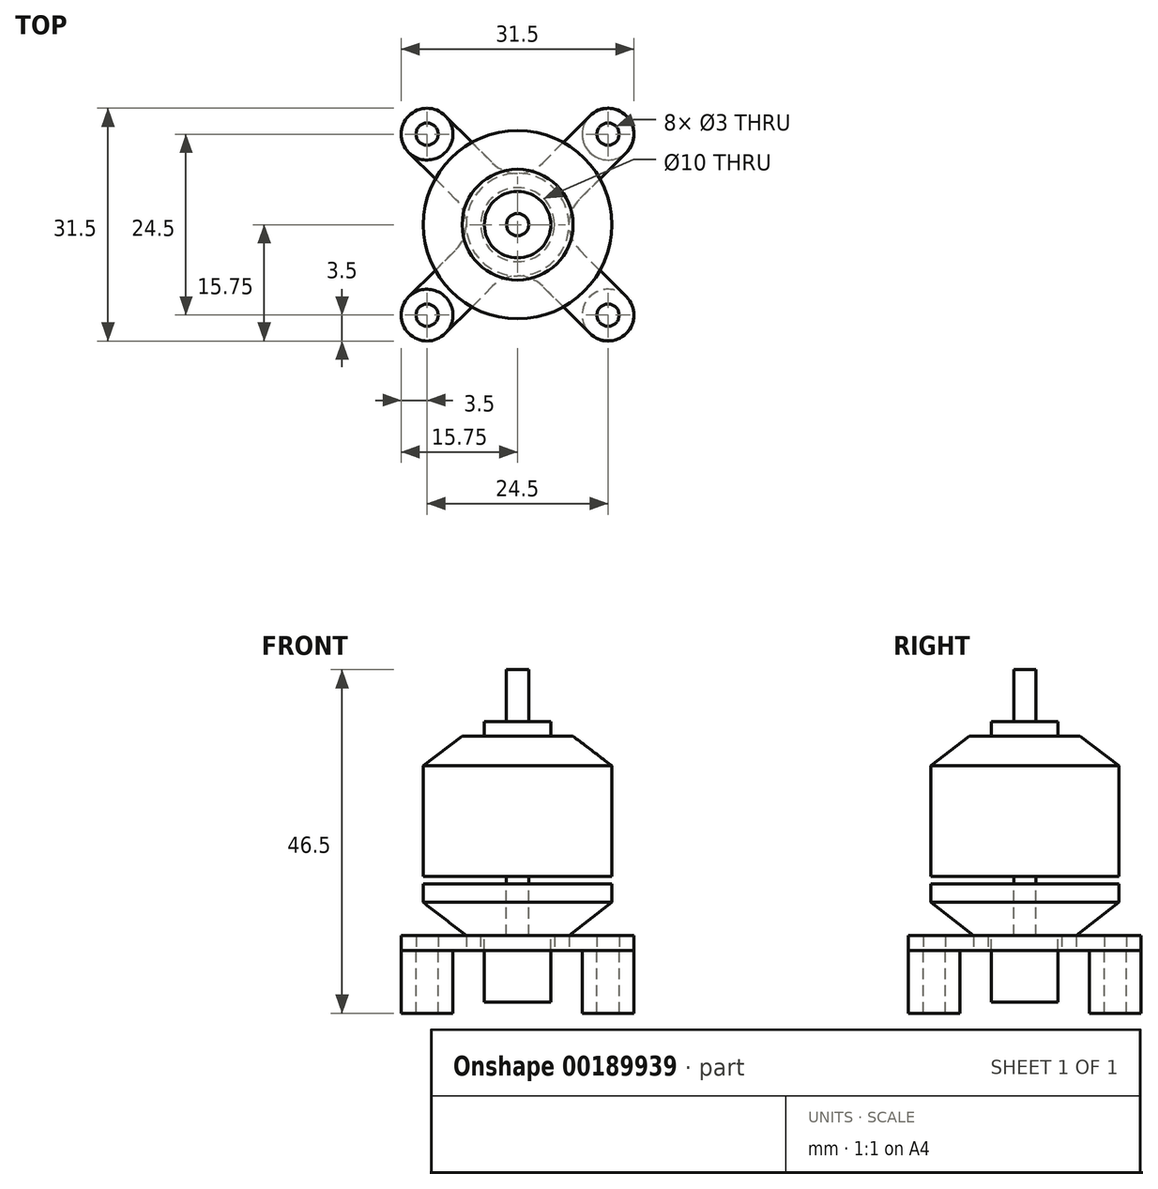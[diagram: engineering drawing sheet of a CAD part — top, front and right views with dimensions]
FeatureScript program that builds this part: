
annotation { "Feature Type Name" : "Feature", "Feature Type Description" : "" }
export const myFeature = defineFeature(function(context is Context, id is Id, definition is map)
    precondition{}
    {
        {
            var Q0;
            Q0=qCreatedBy(makeId("Top.planeOp"),FACE);
            var sketch = newSketch(context, id + "F0", { "sketchPlane" : qUnion([Q0])});
            skLineSegment(sketch, "E0", {"start": v(3.41, 8.36) * mm, "end": v(9.78, 14.72) * mm});
            skLineSegment(sketch, "E1", {"start": v(14.72, 9.78) * mm, "end": v(8.36, 3.41) * mm});
            skArc(sketch, "E2", {"start": v(9.78, 14.72) * mm, "mid": v(14.72, 14.72) * mm, "end": v(14.72, 9.78) * mm});
            skCircle(sketch, "E3", {"center": v(12.25, 12.25) * mm, "radius": 1.5 * mm});
            skLineSegment(sketch, "E4", {"start": v(12.25, 12.25) * mm, "end": v(12.25, 0) * mm, "construction": true});
            skLineSegment(sketch, "E5", {"start": v(12.25, 12.25) * mm, "end": v(0, 12.25) * mm, "construction": true});
            skLineSegment(sketch, "E6.1.0", {"start": v(-8.36, 3.41) * mm, "end": v(-14.72, 9.78) * mm});
            skArc(sketch, "E6.1.1", {"start": v(-14.72, 9.78) * mm, "mid": v(-14.72, 14.72) * mm, "end": v(-9.78, 14.72) * mm});
            skLineSegment(sketch, "E6.1.2", {"start": v(-9.78, 14.72) * mm, "end": v(-3.41, 8.36) * mm});
            skCircle(sketch, "E6.1.3", {"center": v(-12.25, 12.25) * mm, "radius": 1.5 * mm});
            skLineSegment(sketch, "E6.2.0", {"start": v(-3.41, -8.36) * mm, "end": v(-9.78, -14.72) * mm});
            skArc(sketch, "E6.2.1", {"start": v(-9.78, -14.72) * mm, "mid": v(-14.72, -14.72) * mm, "end": v(-14.72, -9.78) * mm});
            skLineSegment(sketch, "E6.2.2", {"start": v(-14.72, -9.78) * mm, "end": v(-8.36, -3.41) * mm});
            skCircle(sketch, "E6.2.3", {"center": v(-12.25, -12.25) * mm, "radius": 1.5 * mm});
            skLineSegment(sketch, "E6.3.0", {"start": v(8.36, -3.41) * mm, "end": v(14.72, -9.78) * mm});
            skArc(sketch, "E6.3.1", {"start": v(14.72, -9.78) * mm, "mid": v(14.72, -14.72) * mm, "end": v(9.78, -14.72) * mm});
            skLineSegment(sketch, "E6.3.2", {"start": v(9.78, -14.72) * mm, "end": v(3.41, -8.36) * mm});
            skCircle(sketch, "E6.3.3", {"center": v(12.25, -12.25) * mm, "radius": 1.5 * mm});
            skPoint(sketch, "E6.center", {"position": v(0, 0) * mm});
            skCircle(sketch, "E7", {"center": v(0, 0) * mm, "radius": 5 * mm});
            skPoint(sketch, "E8.visualSharp", {"position": v(0, 4.95) * mm});
            skArc(sketch, "E8.filletArc", {"start": v(-3.41, 8.36) * mm, "mid": v(0, 6.95) * mm, "end": v(3.41, 8.36) * mm});
            skPoint(sketch, "E9.visualSharp", {"position": v(4.95, 0) * mm});
            skArc(sketch, "E9.filletArc", {"start": v(8.36, 3.41) * mm, "mid": v(6.95, 0) * mm, "end": v(8.36, -3.41) * mm});
            skPoint(sketch, "E10.visualSharp", {"position": v(0, -4.95) * mm});
            skArc(sketch, "E10.filletArc", {"start": v(3.41, -8.36) * mm, "mid": v(0, -6.95) * mm, "end": v(-3.41, -8.36) * mm});
            skPoint(sketch, "E11.visualSharp", {"position": v(-4.95, 0) * mm});
            skArc(sketch, "E11.filletArc", {"start": v(-8.36, -3.41) * mm, "mid": v(-6.95, 0) * mm, "end": v(-8.36, 3.41) * mm});
            skSolve(sketch);
        }
        {
            var Q0;
            Q0=makeQuery(id+"F0.imprint","IMPRINT",FACE,{"disambiguationData":[TD([[makeQuery(id+"F0.imprint","IMPRINT",EDGE,{"derivedFrom":sQuery(id+"F0.wireOp",EDGE,"E0")}),-1.0]])]});
            extrude(context, id + "F1", {"entities" : qUnion([Q0]), "depth" : 2 * mm});
        }
        {
            var Q0;
            Q0=qCreatedBy(makeId("Front.planeOp"),FACE);
            var sketch = newSketch(context, id + "F2", { "sketchPlane" : qUnion([Q0])});
            skLineSegment(sketch, "E12", {"start": v(12.75, 25) * mm, "end": v(12.75, 10) * mm});
            skLineSegment(sketch, "E13", {"start": v(12.75, 10) * mm, "end": v(1.5, 10) * mm});
            skLineSegment(sketch, "E14", {"start": v(1.5, 10) * mm, "end": v(1.5, 2) * mm});
            skLineSegment(sketch, "E15", {"start": v(1.5, 2) * mm, "end": v(4.5, 2) * mm});
            skLineSegment(sketch, "E16", {"start": v(4.5, 2) * mm, "end": v(4.5, -7) * mm});
            skLineSegment(sketch, "E17", {"start": v(4.5, -7) * mm, "end": v(0, -7) * mm});
            skLineSegment(sketch, "E18", {"start": v(1.5, 31) * mm, "end": v(4.5, 31) * mm});
            skLineSegment(sketch, "E19", {"start": v(4.5, 31) * mm, "end": v(4.5, 29) * mm});
            skLineSegment(sketch, "E20", {"start": v(4.5, 29) * mm, "end": v(7.5, 29) * mm});
            skLineSegment(sketch, "E21", {"start": v(7.5, 29) * mm, "end": v(12.75, 25) * mm});
            skLineSegment(sketch, "E22", {"start": v(0, 38) * mm, "end": v(1.5, 38) * mm});
            skLineSegment(sketch, "E23", {"start": v(1.5, 38) * mm, "end": v(1.5, 31) * mm});
            skLineSegment(sketch, "E24", {"start": v(0, 38) * mm, "end": v(0, -7) * mm});
            skSolve(sketch);
        }
        {
            var Q0;
            Q0=makeQuery(id+"F2.imprint","IMPRINT",FACE,{"disambiguationData":[TD([[makeQuery(id+"F2.imprint","IMPRINT",EDGE,{"derivedFrom":sQuery(id+"F2.wireOp",EDGE,"E12")}),-1.0]])]});
            var Q1;
            Q1=sQuery(id+"F2.wireOp",EDGE,"E24");
            revolve(context, id + "F3", {"entities" : qUnion([Q0]), "axis" : qUnion([Q1]), "revolveType" : RevolveType.FULL});
        }
        {
            var Q0;
            Q0=qCreatedBy(makeId("Front.planeOp"),FACE);
            var sketch = newSketch(context, id + "F4", { "sketchPlane" : qUnion([Q0])});
            skLineSegment(sketch, "E25", {"start": v(0, 9) * mm, "end": v(12.75, 9) * mm});
            skLineSegment(sketch, "E26", {"start": v(12.75, 9) * mm, "end": v(12.75, 6.5) * mm});
            skLineSegment(sketch, "E27", {"start": v(12.75, 6.5) * mm, "end": v(6.95, 2) * mm});
            skLineSegment(sketch, "E28", {"start": v(6.95, 2) * mm, "end": v(0, 2) * mm});
            skLineSegment(sketch, "E29", {"start": v(0, 2) * mm, "end": v(0, 9) * mm});
            skLineSegment(sketch, "E30", {"start": v(12.75, 25) * mm, "end": v(12.75, 10) * mm, "construction": true});
            skLineSegment(sketch, "E31", {"start": v(-12.75, 10) * mm, "end": v(-12.75, 25) * mm, "construction": true});
            skPoint(sketch, "E32.0", {"position": v(6.95, 2) * mm});
            skSolve(sketch);
        }
        {
            var Q0;
            Q0=makeQuery(id+"F4.imprint","IMPRINT",FACE,{"disambiguationData":[TD([[makeQuery(id+"F4.imprint","IMPRINT",EDGE,{"derivedFrom":sQuery(id+"F4.wireOp",EDGE,"E25")}),-1.0]])]});
            var Q1;
            Q1=sQuery(id+"F4.wireOp",EDGE,"E29");
            revolve(context, id + "F5", {"entities" : qUnion([Q0]), "axis" : qUnion([Q1]), "revolveType" : RevolveType.FULL});
        }
        {
            var Q0;
            Q0=makeQuery(id+"F1.opExtrude","CAP_FACE",FACE,{"disambiguationData":[OSD([sQuery(id+"F0.wireOp",EDGE,"E0"),sQuery(id+"F0.wireOp",EDGE,"E1"),sQuery(id+"F0.wireOp",EDGE,"E2"),sQuery(id+"F0.wireOp",EDGE,"E3"),sQuery(id+"F0.wireOp",EDGE,"E6.1.0"),sQuery(id+"F0.wireOp",EDGE,"E6.1.1"),sQuery(id+"F0.wireOp",EDGE,"E6.1.2"),sQuery(id+"F0.wireOp",EDGE,"E6.1.3"),sQuery(id+"F0.wireOp",EDGE,"E6.2.0"),sQuery(id+"F0.wireOp",EDGE,"E6.2.1"),sQuery(id+"F0.wireOp",EDGE,"E6.2.2"),sQuery(id+"F0.wireOp",EDGE,"E6.2.3"),sQuery(id+"F0.wireOp",EDGE,"E6.3.0"),sQuery(id+"F0.wireOp",EDGE,"E6.3.1"),sQuery(id+"F0.wireOp",EDGE,"E6.3.2"),sQuery(id+"F0.wireOp",EDGE,"E6.3.3"),sQuery(id+"F0.wireOp",EDGE,"E7"),sQuery(id+"F0.wireOp",EDGE,"E8.filletArc"),sQuery(id+"F0.wireOp",EDGE,"E9.filletArc"),sQuery(id+"F0.wireOp",EDGE,"E10.filletArc"),sQuery(id+"F0.wireOp",EDGE,"E11.filletArc")])],"isStart":true});
            var sketch = newSketch(context, id + "F6", { "sketchPlane" : qUnion([Q0])});
            skCircle(sketch, "E33", {"center": v(12.25, 12.25) * mm, "radius": 3.5 * mm});
            skCircle(sketch, "E34", {"center": v(12.25, -12.25) * mm, "radius": 3.5 * mm});
            skCircle(sketch, "E35", {"center": v(-12.25, -12.25) * mm, "radius": 3.5 * mm});
            skCircle(sketch, "E36", {"center": v(-12.25, 12.25) * mm, "radius": 3.5 * mm});
            skCircle(sketch, "E37", {"center": v(12.25, 12.25) * mm, "radius": 1.5 * mm});
            skCircle(sketch, "E38", {"center": v(12.25, -12.25) * mm, "radius": 1.5 * mm});
            skCircle(sketch, "E39", {"center": v(-12.25, -12.25) * mm, "radius": 1.5 * mm});
            skCircle(sketch, "E40", {"center": v(-12.25, 12.25) * mm, "radius": 1.5 * mm});
            skSolve(sketch);
        }
        {
            var Q0;
            Q0 = qSketchRegion(id + "F6", true);
            extrude(context, id + "F7", {"entities" : qUnion([Q0]), "depth" : 8.5 * mm});
        }
    });
